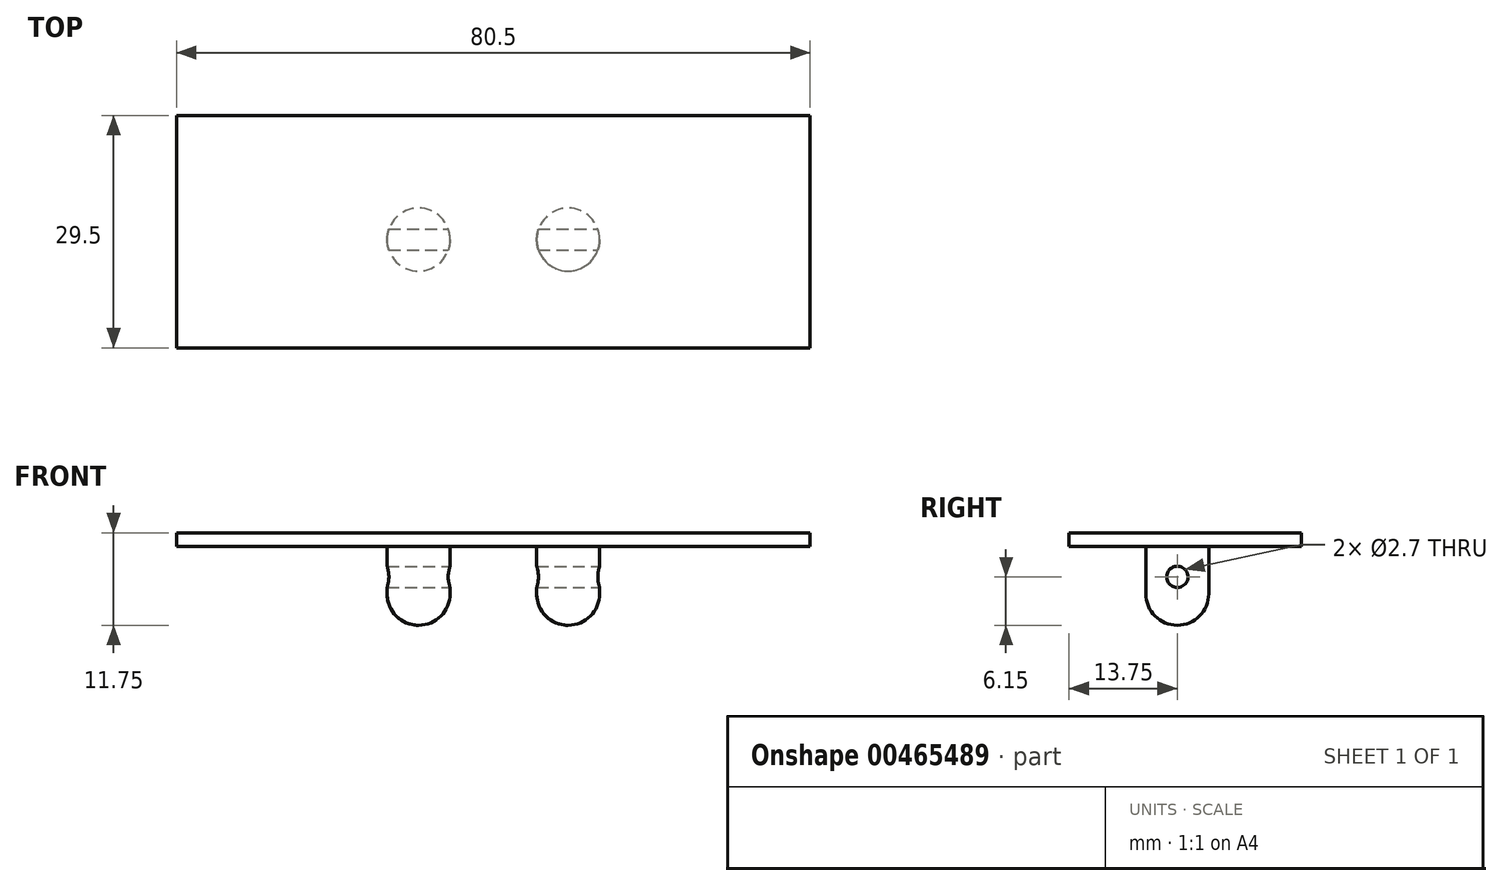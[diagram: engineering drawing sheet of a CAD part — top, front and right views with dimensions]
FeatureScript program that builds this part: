
annotation { "Feature Type Name" : "Feature", "Feature Type Description" : "" }
export const myFeature = defineFeature(function(context is Context, id is Id, definition is map)
    precondition{}
    {
        {
            var Q0;
            Q0=qCreatedBy(makeId("Top.planeOp"),FACE);
            var sketch = newSketch(context, id + "F0", { "sketchPlane" : qUnion([Q0])});
            skLineSegment(sketch, "E0.bottom", {"start": v(0, 0) * mm, "end": v(-88, 0) * mm});
            skLineSegment(sketch, "E0.top", {"start": v(0, 37) * mm, "end": v(-88, 37) * mm});
            skLineSegment(sketch, "E0.left", {"start": v(0, 0) * mm, "end": v(0, 37) * mm});
            skLineSegment(sketch, "E0.right", {"start": v(-88, 0) * mm, "end": v(-88, 37) * mm});
            skSolve(sketch);
        }
        {
            var Q0;
            Q0=qSketchRegion(id+"F0",true);
            extrude(context, id + "F1", {"entities" : qUnion([Q0]), "depth" : 1.75 * mm, "offsetDistance" : 25 * mm});
        }
        {
            var Q0;
            Q0=makeQuery(id+"F1.opExtrude","CAP_FACE",FACE,{"disambiguationData":[OSD([sQuery(id+"F0.wireOp",EDGE,"E0.bottom"),sQuery(id+"F0.wireOp",EDGE,"E0.top"),sQuery(id+"F0.wireOp",EDGE,"E0.left"),sQuery(id+"F0.wireOp",EDGE,"E0.right")])],"isStart":false});
            var sketch = newSketch(context, id + "F2", { "sketchPlane" : qUnion([Q0])});
            skLineSegment(sketch, "E1.bottom", {"start": v(-84.25, 33.25) * mm, "end": v(-3.75, 33.25) * mm});
            skLineSegment(sketch, "E1.top", {"start": v(-84.25, 3.75) * mm, "end": v(-3.75, 3.75) * mm});
            skLineSegment(sketch, "E1.left", {"start": v(-84.25, 33.25) * mm, "end": v(-84.25, 3.75) * mm});
            skLineSegment(sketch, "E1.right", {"start": v(-3.75, 33.25) * mm, "end": v(-3.75, 3.75) * mm});
            skSolve(sketch);
        }
        {
            var Q0;
            Q0=qSketchRegion(id+"F2",true);
            extrude(context, id + "F3", {"entities" : qUnion([Q0]), "operationType" : NewBodyOperationType.ADD, "depth" : 1.5 * mm, "offsetDistance" : 25 * mm});
        }
        {
            var Q0;
            Q0=makeQuery(id+"F1.opExtrude","CAP_FACE",FACE,{"disambiguationData":[OSD([sQuery(id+"F0.wireOp",EDGE,"E0.bottom"),sQuery(id+"F0.wireOp",EDGE,"E0.top"),sQuery(id+"F0.wireOp",EDGE,"E0.left"),sQuery(id+"F0.wireOp",EDGE,"E0.right")])],"isStart":true});
            var sketch = newSketch(context, id + "F4", { "sketchPlane" : qUnion([Q0])});
            skCircle(sketch, "E2", {"center": v(-53.5, -17.5) * mm, "radius": 4 * mm});
            skLineSegment(sketch, "E3", {"start": v(-44, 0) * mm, "end": v(-44, -37) * mm, "construction": true});
            skCircle(sketch, "E4.MirrorC", {"center": v(-34.5, -17.5) * mm, "radius": 4 * mm});
            skSolve(sketch);
        }
        {
            var Q0;
            Q0=qSketchRegion(id+"F4",true);
            extrude(context, id + "F5", {"entities" : qUnion([Q0]), "operationType" : NewBodyOperationType.ADD, "depth" : 10 * mm});
        }
        {
            var Q0;
            Q0=makeQuery(id+"F5.opExtrude","CAP_EDGE",EDGE,{"disambiguationData":[OSD([sQuery(id+"F4.wireOp",EDGE,"E2")])],"isStart":false});
            var Q1;
            Q1=makeQuery(id+"F5.opExtrude","CAP_EDGE",EDGE,{"disambiguationData":[OSD([sQuery(id+"F4.wireOp",EDGE,"E4.MirrorC")])],"isStart":false});
            fillet(context, id + "F6", {"entities" : qUnion([Q0, Q1]), "radius" : 4 * mm, "tangentPropagation" : true, "allowEdgeOverflow" : false});
        }
        {
            var Q0;
            Q0=makeQuery(id+"F52yH6P0KQi80XE_1.boolean.opBoolean","MERGE",FACE,{"derivedFrom":[makeQuery(id+"F1.opExtrude","SWEPT_FACE",FACE,{"disambiguationData":[OSD([sQuery(id+"F0.wireOp",EDGE,"E0.left")])]}),makeQuery(id+"F52yH6P0KQi80XE_1.opExtrude","SWEPT_FACE",FACE,{"disambiguationData":[OSD([sQuery(id+"FGr434h4xjwXrtd_1.wireOp",EDGE,"zj5YKJeh-aPVd-Q5X6-8lwT-vVkT89wnBvyn.right")])]})]});
            var sketch = newSketch(context, id + "F7", { "sketchPlane" : qUnion([Q0])});
            skCircle(sketch, "E5", {"center": v(17.5, -3.85) * mm, "radius": 1.35 * mm});
            skSolve(sketch);
        }
        {
            var Q0;
            Q0=qSketchRegion(id+"F7",true);
            extrude(context, id + "F8", {"entities" : qUnion([Q0]), "operationType" : NewBodyOperationType.REMOVE, "endBound" : BoundingType.THROUGH_ALL, "oppositeDirection" : true, "depth" : 25 * mm});
        }
        {
            var Q0;
            Q0=makeQuery(id+"F1.opExtrude","SWEPT_EDGE",EDGE,{"disambiguationData":[OSD([sQuery(id+"F0.wireOp",EDGE,"E0.bottom"),sQuery(id+"F0.wireOp",EDGE,"E0.right")])]});
            var Q1;
            Q1=makeQuery(id+"F1.opExtrude","SWEPT_EDGE",EDGE,{"disambiguationData":[OSD([sQuery(id+"F0.wireOp",EDGE,"E0.top"),sQuery(id+"F0.wireOp",EDGE,"E0.right")])]});
            var Q2;
            Q2=makeQuery(id+"F1.opExtrude","SWEPT_EDGE",EDGE,{"disambiguationData":[OSD([sQuery(id+"F0.wireOp",EDGE,"E0.top"),sQuery(id+"F0.wireOp",EDGE,"E0.left")])]});
            var Q3;
            Q3=makeQuery(id+"F1.opExtrude","SWEPT_EDGE",EDGE,{"disambiguationData":[OSD([sQuery(id+"F0.wireOp",EDGE,"E0.bottom"),sQuery(id+"F0.wireOp",EDGE,"E0.left")])]});
            fillet(context, id + "F9", {"entities" : qUnion([Q0, Q1, Q2, Q3]), "radius" : 3 * mm, "tangentPropagation" : true, "allowEdgeOverflow" : false});
        }
        {
            var Q0;
            Q0 = qSketchRegion(id + "F2", true);
            extrude(context, id + "F10", {"entities" : qUnion([Q0]), "operationType" : NewBodyOperationType.INTERSECT, "oppositeDirection" : true, "depth" : 25 * mm, "offsetDistance" : 25 * mm});
        }
    });
